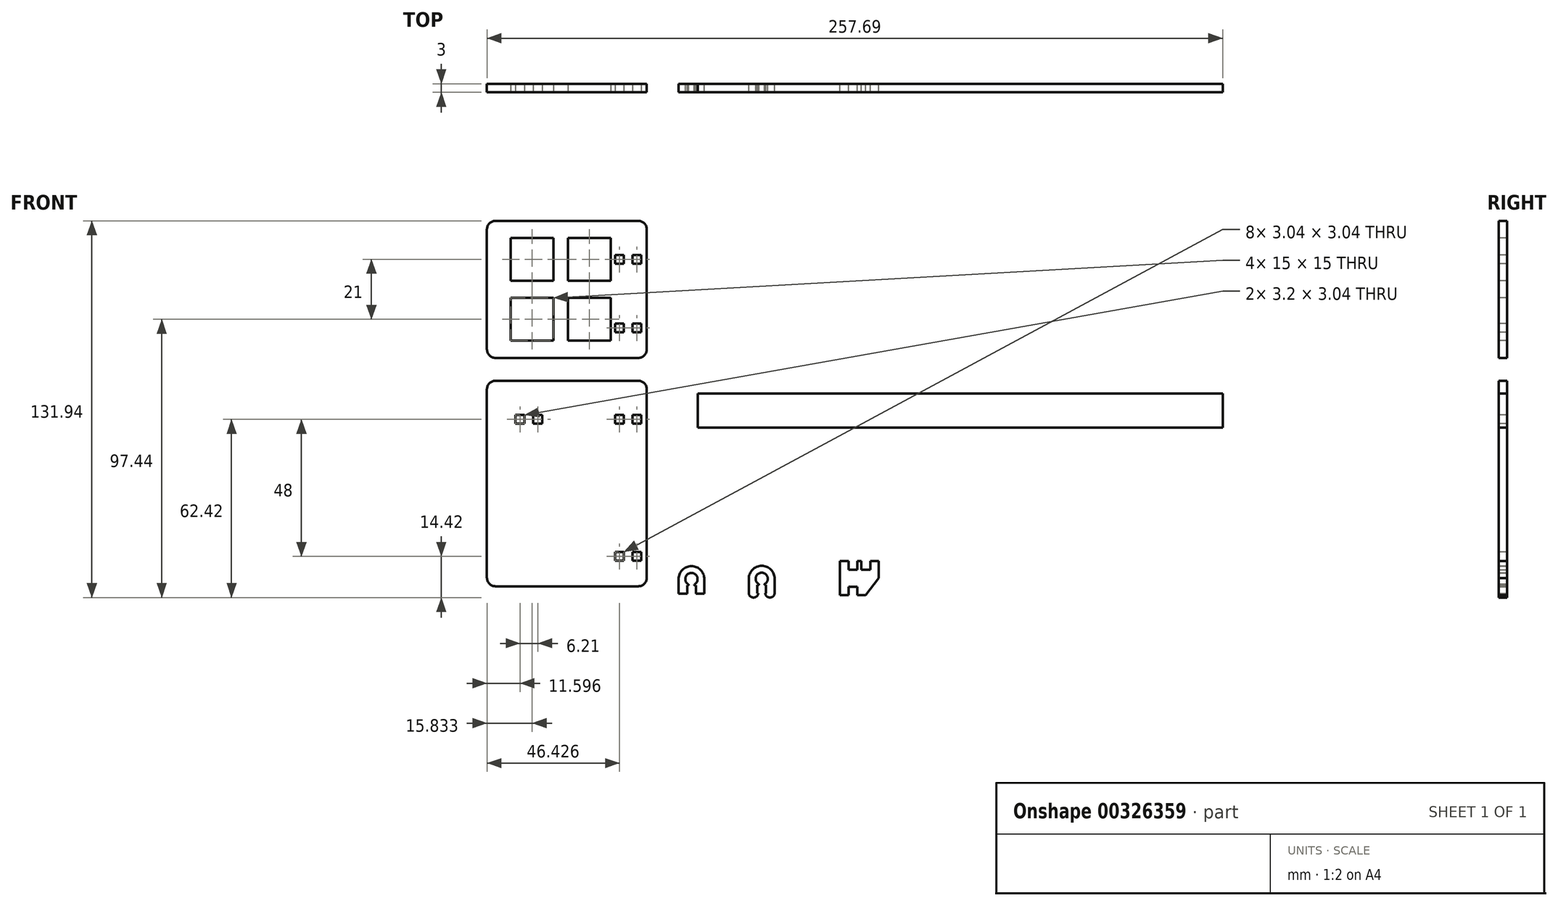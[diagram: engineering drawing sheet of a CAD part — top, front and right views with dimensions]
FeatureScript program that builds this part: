
annotation { "Feature Type Name" : "Feature", "Feature Type Description" : "" }
export const myFeature = defineFeature(function(context is Context, id is Id, definition is map)
    precondition{}
    {
        {
            var Q0;
            Q0=qCreatedBy(makeId("Front.planeOp"),FACE);
            var sketch = newSketch(context, id + "F0", { "sketchPlane" : qUnion([Q0])});
            skArc(sketch, "E0", {"start": v(1.01, 0.63) * mm, "mid": v(0.03, 4.67) * mm, "end": v(-1.07, 0.66) * mm});
            skPoint(sketch, "E0.centerSnap0", {"position": v(-1.52, 2.52) * mm});
            skArc(sketch, "E1", {"start": v(4.53, 2.52) * mm, "mid": v(0, 7.05) * mm, "end": v(-4.53, 2.52) * mm});
            skLineSegment(sketch, "E2", {"start": v(-4.53, 2.52) * mm, "end": v(-4.53, -2.63) * mm});
            skLineSegment(sketch, "E3", {"start": v(4.52, 2.52) * mm, "end": v(4.53, -2.63) * mm});
            skPoint(sketch, "E3.startSnap0", {"position": v(1.52, 2.52) * mm});
            skPoint(sketch, "E4.orphan", {"position": v(-1.52, 4.05) * mm});
            skPoint(sketch, "E5.orphan", {"position": v(1.52, 4.05) * mm});
            skLineSegment(sketch, "E6", {"start": v(-1.08, 0.37) * mm, "end": v(-1.52, 0.37) * mm});
            skLineSegment(sketch, "E7", {"start": v(1.07, 0.37) * mm, "end": v(1.53, 0.37) * mm});
            skArc(sketch, "E8", {"start": v(-1.08, 0.37) * mm, "mid": v(-1, 0.52) * mm, "end": v(-1.08, 0.67) * mm});
            skArc(sketch, "E9", {"start": v(1.01, 0.63) * mm, "mid": v(0.96, 0.47) * mm, "end": v(1.1, 0.37) * mm});
            skPoint(sketch, "E10.orphan", {"position": v(0, 0.37) * mm});
            skPoint(sketch, "E11.start.orphan", {"position": v(-2.15, 2.53) * mm});
            skPoint(sketch, "E12.start.orphan", {"position": v(2.15, 2.53) * mm});
            skLineSegment(sketch, "E13", {"start": v(-1.52, -2.63) * mm, "end": v(-1.52, 0.37) * mm});
            skLineSegment(sketch, "E14", {"start": v(1.53, -2.63) * mm, "end": v(1.53, 0.38) * mm});
            skPoint(sketch, "E15", {"position": v(-1.52, -2.63) * mm});
            skPoint(sketch, "E16", {"position": v(1.53, -2.63) * mm});
            skLineSegment(sketch, "E17", {"start": v(-1.52, -2.63) * mm, "end": v(-4.53, -2.63) * mm});
            skLineSegment(sketch, "E18", {"start": v(1.53, -2.63) * mm, "end": v(4.53, -2.63) * mm});
            skPoint(sketch, "E19.start.orphan", {"position": v(0, 4.05) * mm});
            skArc(sketch, "E20", {"start": v(25.62, 0.77) * mm, "mid": v(24.65, 4.77) * mm, "end": v(23.55, 0.8) * mm});
            skPoint(sketch, "E20.centerSnap0", {"position": v(23.09, 2.64) * mm});
            skArc(sketch, "E21", {"start": v(29.14, 2.67) * mm, "mid": v(24.6, 7.17) * mm, "end": v(20.09, 2.64) * mm});
            skLineSegment(sketch, "E22", {"start": v(20.09, 2.64) * mm, "end": v(20.09, -2.5) * mm});
            skLineSegment(sketch, "E23", {"start": v(29.14, 2.67) * mm, "end": v(29.14, -2.48) * mm});
            skPoint(sketch, "E23.startSnap0", {"position": v(26.14, 2.67) * mm});
            skPoint(sketch, "E24.orphan", {"position": v(23.08, 4.16) * mm});
            skPoint(sketch, "E25.orphan", {"position": v(26.12, 4.15) * mm});
            skLineSegment(sketch, "E26", {"start": v(23.55, 0.52) * mm, "end": v(23.09, 0.52) * mm});
            skLineSegment(sketch, "E27", {"start": v(25.68, 0.52) * mm, "end": v(26.14, 0.52) * mm});
            skArc(sketch, "E28", {"start": v(23.55, 0.52) * mm, "mid": v(23.63, 0.66) * mm, "end": v(23.55, 0.8) * mm});
            skArc(sketch, "E29", {"start": v(25.62, 0.77) * mm, "mid": v(25.56, 0.61) * mm, "end": v(25.7, 0.52) * mm});
            skPoint(sketch, "E30.orphan", {"position": v(24.61, 0.52) * mm});
            skPoint(sketch, "E31.start.orphan", {"position": v(22.49, 2.64) * mm});
            skPoint(sketch, "E32.start.orphan", {"position": v(26.74, 2.67) * mm});
            skLineSegment(sketch, "E33", {"start": v(23.09, -2.48) * mm, "end": v(23.09, 0.52) * mm});
            skLineSegment(sketch, "E34", {"start": v(26.14, -2.48) * mm, "end": v(26.14, 0.52) * mm});
            skPoint(sketch, "E35", {"position": v(23.09, -2.48) * mm});
            skPoint(sketch, "E36", {"position": v(26.14, -2.48) * mm});
            skPoint(sketch, "E37.start.orphan", {"position": v(24.6, 4.15) * mm});
            skPoint(sketch, "E38.end.orphan", {"position": v(23.09, -3.5) * mm});
            skPoint(sketch, "E39.orphan", {"position": v(26.14, -3.48) * mm});
            skLineSegment(sketch, "E40", {"start": v(23.09, -2.48) * mm, "end": v(23.39, -2.48) * mm});
            skLineSegment(sketch, "E41", {"start": v(26.14, -2.48) * mm, "end": v(25.84, -2.48) * mm});
            skArc(sketch, "E42", {"start": v(20.09, -2.5) * mm, "mid": v(21.74, -3.94) * mm, "end": v(23.39, -2.48) * mm});
            skArc(sketch, "E43", {"start": v(25.84, -2.48) * mm, "mid": v(27.49, -3.94) * mm, "end": v(29.14, -2.48) * mm});
            skLineSegment(sketch, "E44", {"start": v(61.04, -3.15) * mm, "end": v(58.06, -3.15) * mm});
            skLineSegment(sketch, "E45", {"start": v(58.06, -3.15) * mm, "end": v(58.06, -0.13) * mm});
            skLineSegment(sketch, "E46", {"start": v(58.06, -0.13) * mm, "end": v(55.02, -0.13) * mm});
            skLineSegment(sketch, "E47", {"start": v(55.02, -0.13) * mm, "end": v(55.02, -3.15) * mm});
            skLineSegment(sketch, "E48", {"start": v(55.02, -3.15) * mm, "end": v(52.04, -3.15) * mm});
            skLineSegment(sketch, "E49", {"start": v(52.04, -3.15) * mm, "end": v(52.04, 8.85) * mm});
            skLineSegment(sketch, "E50", {"start": v(52.04, 8.85) * mm, "end": v(55.02, 8.85) * mm});
            skLineSegment(sketch, "E51", {"start": v(55.02, 8.85) * mm, "end": v(55.02, 5.83) * mm});
            skLineSegment(sketch, "E52", {"start": v(55.02, 5.83) * mm, "end": v(58.06, 5.83) * mm});
            skLineSegment(sketch, "E53", {"start": v(58.06, 5.83) * mm, "end": v(58.06, 8.85) * mm});
            skLineSegment(sketch, "E54", {"start": v(58.06, 8.85) * mm, "end": v(59.5, 8.85) * mm});
            skPoint(sketch, "E55", {"position": v(59.5, 8.85) * mm});
            skPoint(sketch, "E56", {"position": v(59.5, -3.15) * mm});
            skPoint(sketch, "E57", {"position": v(62.6, 8.85) * mm});
            skPoint(sketch, "E58.orphan", {"position": v(61.04, 8.85) * mm});
            skLineSegment(sketch, "E59", {"start": v(62.6, 8.85) * mm, "end": v(65.6, 8.85) * mm});
            skLineSegment(sketch, "E60", {"start": v(65.6, 8.85) * mm, "end": v(65.6, 2.85) * mm});
            skLineSegment(sketch, "E61", {"start": v(65.6, 2.85) * mm, "end": v(61.04, -3.15) * mm});
            skLineSegment(sketch, "E62", {"start": v(59.5, 8.85) * mm, "end": v(59.5, 5.81) * mm});
            skLineSegment(sketch, "E63", {"start": v(59.5, 5.81) * mm, "end": v(62.6, 5.81) * mm});
            skLineSegment(sketch, "E64", {"start": v(62.6, 5.81) * mm, "end": v(62.6, 8.85) * mm});
            skSolve(sketch);
        }
        {
            var Q0;
            Q0=makeQuery(id+"F0.imprint","IMPRINT",FACE,{"disambiguationData":[TD([[makeQuery(id+"F0.imprint","IMPRINT",EDGE,{"derivedFrom":sQuery(id+"F0.wireOp",EDGE,"E0")}),-1.0]])]});
            var Q1;
            {var subQ1=sQuery(id+"F0.wireOp",EDGE,"E20");Q1=makeQuery(id+"F0.imprint","IMPRINT",FACE,{"disambiguationData":[TD([[makeQuery(id+"F0.imprint","IMPRINT",EDGE,{"derivedFrom":subQ1}),-1.0]])]});}
            var Q2;
            Q2=makeQuery(id+"F0.imprint","IMPRINT",FACE,{"disambiguationData":[TD([[makeQuery(id+"F0.imprint","IMPRINT",EDGE,{"derivedFrom":sQuery(id+"F0.wireOp",EDGE,"E44")}),-1.0]])]});
            extrude(context, id + "F1", {"entities" : qUnion([Q0, Q1, Q2]), "depth" : 3 * mm});
        }
        {
            var Q0;
            Q0=qCreatedBy(makeId("Front.planeOp"),FACE);
            var sketch = newSketch(context, id + "F2", { "sketchPlane" : qUnion([Q0])});
            skLineSegment(sketch, "E65.bottom", {"start": v(-71.63, 0) * mm, "end": v(-15.63, 0) * mm});
            skLineSegment(sketch, "E65.left", {"start": v(-71.63, 0) * mm, "end": v(-71.63, 72) * mm});
            skLineSegment(sketch, "E65.right", {"start": v(-15.63, 0) * mm, "end": v(-15.63, 72) * mm});
            skLineSegment(sketch, "E66", {"start": v(-71.63, 80) * mm, "end": v(-71.63, 128) * mm});
            skLineSegment(sketch, "E67", {"start": v(-15.63, 80) * mm, "end": v(-15.63, 128) * mm});
            skLineSegment(sketch, "E68", {"start": v(-15.63, 128) * mm, "end": v(-71.63, 128) * mm});
            skLineSegment(sketch, "E69", {"start": v(-71.63, 72) * mm, "end": v(-15.63, 72) * mm});
            skLineSegment(sketch, "E70", {"start": v(-71.63, 80) * mm, "end": v(-15.63, 80) * mm});
            skSolve(sketch);
        }
        {
            var Q0;
            Q0=makeQuery(id+"F2.imprint","IMPRINT",FACE,{"disambiguationData":[TD([[makeQuery(id+"F2.imprint","IMPRINT",EDGE,{"derivedFrom":sQuery(id+"F2.wireOp",EDGE,"E66")}),-1.0]])]});
            var Q1;
            Q1=makeQuery(id+"F2.imprint","IMPRINT",FACE,{"disambiguationData":[TD([[makeQuery(id+"F2.imprint","IMPRINT",EDGE,{"derivedFrom":sQuery(id+"F2.wireOp",EDGE,"E65.bottom")}),1.0]])]});
            extrude(context, id + "F3", {"entities" : qUnion([Q0, Q1]), "depth" : 3 * mm});
        }
        {
            var Q0;
            Q0=makeQuery(id+"F3.opExtrude","CAP_FACE",FACE,{"disambiguationData":[OSD([sQuery(id+"F2.wireOp",EDGE,"E66"),sQuery(id+"F2.wireOp",EDGE,"E67"),sQuery(id+"F2.wireOp",EDGE,"E68"),sQuery(id+"F2.wireOp",EDGE,"E70")])],"isStart":false});
            var sketch = newSketch(context, id + "F4", { "sketchPlane" : qUnion([Q0])});
            skLineSegment(sketch, "E71.bottom", {"start": v(-23.68, 12) * mm, "end": v(-26.72, 12) * mm});
            skLineSegment(sketch, "E71.top", {"start": v(-23.68, 8.96) * mm, "end": v(-26.72, 8.96) * mm});
            skLineSegment(sketch, "E71.left", {"start": v(-23.68, 12) * mm, "end": v(-23.68, 8.96) * mm});
            skLineSegment(sketch, "E71.right", {"start": v(-26.72, 12) * mm, "end": v(-26.72, 8.96) * mm});
            skLineSegment(sketch, "E72.bottom", {"start": v(-20.67, 12) * mm, "end": v(-17.63, 12) * mm});
            skLineSegment(sketch, "E72.top", {"start": v(-20.67, 8.96) * mm, "end": v(-17.63, 8.96) * mm});
            skLineSegment(sketch, "E72.left", {"start": v(-20.67, 12) * mm, "end": v(-20.67, 8.96) * mm});
            skLineSegment(sketch, "E72.right", {"start": v(-17.63, 12) * mm, "end": v(-17.63, 8.96) * mm});
            skLineSegment(sketch, "E73.bottom", {"start": v(-23.68, 60) * mm, "end": v(-26.72, 60) * mm});
            skLineSegment(sketch, "E73.top", {"start": v(-23.68, 56.96) * mm, "end": v(-26.72, 56.96) * mm});
            skLineSegment(sketch, "E73.left", {"start": v(-23.68, 60) * mm, "end": v(-23.68, 56.96) * mm});
            skLineSegment(sketch, "E73.right", {"start": v(-26.72, 60) * mm, "end": v(-26.72, 56.96) * mm});
            skLineSegment(sketch, "E74.bottom", {"start": v(-20.67, 60) * mm, "end": v(-17.63, 60) * mm});
            skLineSegment(sketch, "E74.top", {"start": v(-20.67, 56.96) * mm, "end": v(-17.63, 56.96) * mm});
            skLineSegment(sketch, "E74.left", {"start": v(-20.67, 60) * mm, "end": v(-20.67, 56.96) * mm});
            skLineSegment(sketch, "E74.right", {"start": v(-17.63, 60) * mm, "end": v(-17.63, 56.96) * mm});
            skLineSegment(sketch, "E75.bottom", {"start": v(-23.68, 92) * mm, "end": v(-26.72, 92) * mm});
            skLineSegment(sketch, "E75.top", {"start": v(-23.68, 88.96) * mm, "end": v(-26.72, 88.96) * mm});
            skLineSegment(sketch, "E75.left", {"start": v(-23.68, 92) * mm, "end": v(-23.68, 88.96) * mm});
            skLineSegment(sketch, "E75.right", {"start": v(-26.72, 92) * mm, "end": v(-26.72, 88.96) * mm});
            skLineSegment(sketch, "E76.bottom", {"start": v(-20.67, 92) * mm, "end": v(-17.63, 92) * mm});
            skLineSegment(sketch, "E76.top", {"start": v(-20.67, 88.96) * mm, "end": v(-17.63, 88.96) * mm});
            skLineSegment(sketch, "E76.left", {"start": v(-20.67, 92) * mm, "end": v(-20.67, 88.96) * mm});
            skLineSegment(sketch, "E76.right", {"start": v(-17.63, 92) * mm, "end": v(-17.63, 88.96) * mm});
            skLineSegment(sketch, "E77.bottom", {"start": v(-23.68, 116) * mm, "end": v(-26.72, 116) * mm});
            skLineSegment(sketch, "E77.top", {"start": v(-23.68, 112.96) * mm, "end": v(-26.72, 112.96) * mm});
            skLineSegment(sketch, "E77.left", {"start": v(-23.68, 116) * mm, "end": v(-23.68, 112.96) * mm});
            skLineSegment(sketch, "E77.right", {"start": v(-26.72, 116) * mm, "end": v(-26.72, 112.96) * mm});
            skLineSegment(sketch, "E78.bottom", {"start": v(-20.67, 116) * mm, "end": v(-17.63, 116) * mm});
            skLineSegment(sketch, "E78.top", {"start": v(-20.67, 112.96) * mm, "end": v(-17.63, 112.96) * mm});
            skLineSegment(sketch, "E78.left", {"start": v(-20.67, 116) * mm, "end": v(-20.67, 112.96) * mm});
            skLineSegment(sketch, "E78.right", {"start": v(-17.63, 116) * mm, "end": v(-17.63, 112.96) * mm});
            skLineSegment(sketch, "E79.bottom", {"start": v(-58.43, 60) * mm, "end": v(-61.63, 60) * mm});
            skLineSegment(sketch, "E79.top", {"start": v(-58.43, 56.96) * mm, "end": v(-61.63, 56.96) * mm});
            skLineSegment(sketch, "E79.left", {"start": v(-58.43, 60) * mm, "end": v(-58.43, 56.96) * mm});
            skLineSegment(sketch, "E79.right", {"start": v(-61.63, 60) * mm, "end": v(-61.63, 56.96) * mm});
            skLineSegment(sketch, "E80.bottom", {"start": v(-55.42, 60) * mm, "end": v(-52.22, 60) * mm});
            skLineSegment(sketch, "E80.top", {"start": v(-55.42, 56.96) * mm, "end": v(-52.22, 56.96) * mm});
            skLineSegment(sketch, "E80.left", {"start": v(-55.42, 60) * mm, "end": v(-55.42, 56.96) * mm});
            skLineSegment(sketch, "E80.right", {"start": v(-52.22, 60) * mm, "end": v(-52.22, 56.96) * mm});
            skSolve(sketch);
        }
        {
            var Q0;
            Q0=makeQuery(id+"F4.imprint","IMPRINT",FACE,{"disambiguationData":[TD([[makeQuery(id+"F4.imprint","IMPRINT",EDGE,{"derivedFrom":sQuery(id+"F4.wireOp",EDGE,"E77.bottom")}),1.0]])]});
            var Q1;
            Q1=makeQuery(id+"F4.imprint","IMPRINT",FACE,{"disambiguationData":[TD([[makeQuery(id+"F4.imprint","IMPRINT",EDGE,{"derivedFrom":sQuery(id+"F4.wireOp",EDGE,"E78.bottom")}),-1.0]])]});
            var Q2;
            Q2=makeQuery(id+"F4.imprint","IMPRINT",FACE,{"disambiguationData":[TD([[makeQuery(id+"F4.imprint","IMPRINT",EDGE,{"derivedFrom":sQuery(id+"F4.wireOp",EDGE,"E75.bottom")}),1.0]])]});
            var Q3;
            Q3=makeQuery(id+"F4.imprint","IMPRINT",FACE,{"disambiguationData":[TD([[makeQuery(id+"F4.imprint","IMPRINT",EDGE,{"derivedFrom":sQuery(id+"F4.wireOp",EDGE,"E76.bottom")}),-1.0]])]});
            var Q4;
            Q4=makeQuery(id+"F4.imprint","IMPRINT",FACE,{"disambiguationData":[TD([[makeQuery(id+"F4.imprint","IMPRINT",EDGE,{"derivedFrom":sQuery(id+"F4.wireOp",EDGE,"E73.bottom")}),1.0]])]});
            var Q5;
            Q5=makeQuery(id+"F4.imprint","IMPRINT",FACE,{"disambiguationData":[TD([[makeQuery(id+"F4.imprint","IMPRINT",EDGE,{"derivedFrom":sQuery(id+"F4.wireOp",EDGE,"E74.bottom")}),-1.0]])]});
            var Q6;
            Q6=makeQuery(id+"F4.imprint","IMPRINT",FACE,{"disambiguationData":[TD([[makeQuery(id+"F4.imprint","IMPRINT",EDGE,{"derivedFrom":sQuery(id+"F4.wireOp",EDGE,"E71.bottom")}),1.0]])]});
            var Q7;
            Q7=makeQuery(id+"F4.imprint","IMPRINT",FACE,{"disambiguationData":[TD([[makeQuery(id+"F4.imprint","IMPRINT",EDGE,{"derivedFrom":sQuery(id+"F4.wireOp",EDGE,"E72.bottom")}),-1.0]])]});
            extrude(context, id + "F5", {"entities" : qUnion([Q0, Q1, Q2, Q3, Q4, Q5, Q6, Q7]), "operationType" : NewBodyOperationType.REMOVE, "endBound" : BoundingType.THROUGH_ALL, "oppositeDirection" : true, "depth" : 25 * mm});
        }
        {
            var Q0;
            Q0=qSketchRegion(id+"F4",true);
            extrude(context, id + "F6", {"entities" : qUnion([Q0]), "operationType" : NewBodyOperationType.REMOVE, "oppositeDirection" : true, "depth" : 25 * mm});
        }
        {
            var Q0;
            Q0=makeQuery(id+"F3.opExtrude","CAP_FACE",FACE,{"disambiguationData":[OSD([sQuery(id+"F2.wireOp",EDGE,"E66"),sQuery(id+"F2.wireOp",EDGE,"E67"),sQuery(id+"F2.wireOp",EDGE,"E68"),sQuery(id+"F2.wireOp",EDGE,"E70")])],"isStart":false});
            var sketch = newSketch(context, id + "F7", { "sketchPlane" : qUnion([Q0])});
            skLineSegment(sketch, "E81.bottom", {"start": v(-63.3, 122) * mm, "end": v(-48.3, 122) * mm});
            skLineSegment(sketch, "E81.top", {"start": v(-63.3, 107) * mm, "end": v(-48.3, 107) * mm});
            skLineSegment(sketch, "E81.left", {"start": v(-63.3, 122) * mm, "end": v(-63.3, 107) * mm});
            skLineSegment(sketch, "E81.right", {"start": v(-48.3, 122) * mm, "end": v(-48.3, 107) * mm});
            skLineSegment(sketch, "E82.bottom", {"start": v(-43.3, 122) * mm, "end": v(-28.3, 122) * mm});
            skLineSegment(sketch, "E82.top", {"start": v(-43.3, 107) * mm, "end": v(-28.3, 107) * mm});
            skLineSegment(sketch, "E82.left", {"start": v(-43.3, 122) * mm, "end": v(-43.3, 107) * mm});
            skLineSegment(sketch, "E82.right", {"start": v(-28.3, 122) * mm, "end": v(-28.3, 107) * mm});
            skLineSegment(sketch, "E83.bottom", {"start": v(-63.3, 101) * mm, "end": v(-48.3, 101) * mm});
            skLineSegment(sketch, "E83.top", {"start": v(-63.3, 86) * mm, "end": v(-48.3, 86) * mm});
            skLineSegment(sketch, "E83.left", {"start": v(-63.3, 101) * mm, "end": v(-63.3, 86) * mm});
            skLineSegment(sketch, "E83.right", {"start": v(-48.3, 101) * mm, "end": v(-48.3, 86) * mm});
            skLineSegment(sketch, "E84.bottom", {"start": v(-43.3, 101) * mm, "end": v(-28.3, 101) * mm});
            skLineSegment(sketch, "E84.top", {"start": v(-43.3, 86) * mm, "end": v(-28.3, 86) * mm});
            skLineSegment(sketch, "E84.left", {"start": v(-43.3, 101) * mm, "end": v(-43.3, 86) * mm});
            skLineSegment(sketch, "E84.right", {"start": v(-28.3, 101) * mm, "end": v(-28.3, 86) * mm});
            skSolve(sketch);
        }
        {
            var Q0;
            Q0=makeQuery(id+"F7.imprint","IMPRINT",FACE,{"disambiguationData":[TD([[makeQuery(id+"F7.imprint","IMPRINT",EDGE,{"derivedFrom":sQuery(id+"F7.wireOp",EDGE,"E81.bottom")}),-1.0]])]});
            var Q1;
            Q1=makeQuery(id+"F7.imprint","IMPRINT",FACE,{"disambiguationData":[TD([[makeQuery(id+"F7.imprint","IMPRINT",EDGE,{"derivedFrom":sQuery(id+"F7.wireOp",EDGE,"E82.bottom")}),-1.0]])]});
            var Q2;
            Q2=makeQuery(id+"F7.imprint","IMPRINT",FACE,{"disambiguationData":[TD([[makeQuery(id+"F7.imprint","IMPRINT",EDGE,{"derivedFrom":sQuery(id+"F7.wireOp",EDGE,"E84.bottom")}),-1.0]])]});
            var Q3;
            Q3=makeQuery(id+"F7.imprint","IMPRINT",FACE,{"disambiguationData":[TD([[makeQuery(id+"F7.imprint","IMPRINT",EDGE,{"derivedFrom":sQuery(id+"F7.wireOp",EDGE,"E83.bottom")}),-1.0]])]});
            extrude(context, id + "F8", {"entities" : qUnion([Q0, Q1, Q2, Q3]), "operationType" : NewBodyOperationType.REMOVE, "endBound" : BoundingType.THROUGH_ALL, "oppositeDirection" : true, "depth" : 25 * mm});
        }
        {
            var Q0;
            Q0=makeQuery(id+"F3.opExtrude","SWEPT_EDGE",EDGE,{"disambiguationData":[OSD([sQuery(id+"F2.wireOp",EDGE,"E66"),sQuery(id+"F2.wireOp",EDGE,"E68")])]});
            var Q1;
            Q1=makeQuery(id+"F3.opExtrude","SWEPT_EDGE",EDGE,{"disambiguationData":[OSD([sQuery(id+"F2.wireOp",EDGE,"E65.left"),sQuery(id+"F2.wireOp",EDGE,"E69")])]});
            var Q2;
            Q2=makeQuery(id+"F3.opExtrude","SWEPT_EDGE",EDGE,{"disambiguationData":[OSD([sQuery(id+"F2.wireOp",EDGE,"E65.right"),sQuery(id+"F2.wireOp",EDGE,"E69")])]});
            var Q3;
            Q3=makeQuery(id+"F3.opExtrude","SWEPT_EDGE",EDGE,{"disambiguationData":[OSD([sQuery(id+"F2.wireOp",EDGE,"E66"),sQuery(id+"F2.wireOp",EDGE,"E70")])]});
            var Q4;
            Q4=makeQuery(id+"F3.opExtrude","SWEPT_EDGE",EDGE,{"disambiguationData":[OSD([sQuery(id+"F2.wireOp",EDGE,"E67"),sQuery(id+"F2.wireOp",EDGE,"E70")])]});
            var Q5;
            Q5=makeQuery(id+"F3.opExtrude","SWEPT_EDGE",EDGE,{"disambiguationData":[OSD([sQuery(id+"F2.wireOp",EDGE,"E67"),sQuery(id+"F2.wireOp",EDGE,"E68")])]});
            var Q6;
            Q6=makeQuery(id+"F3.opExtrude","SWEPT_EDGE",EDGE,{"disambiguationData":[OSD([sQuery(id+"F2.wireOp",EDGE,"E65.bottom"),sQuery(id+"F2.wireOp",EDGE,"E65.left")])]});
            var Q7;
            Q7=makeQuery(id+"F3.opExtrude","SWEPT_EDGE",EDGE,{"disambiguationData":[OSD([sQuery(id+"F2.wireOp",EDGE,"E65.bottom"),sQuery(id+"F2.wireOp",EDGE,"E65.right")])]});
            fillet(context, id + "F9", {"entities" : qUnion([Q0, Q1, Q2, Q3, Q4, Q5, Q6, Q7]), "radius" : 3 * mm, "tangentPropagation" : true, "allowEdgeOverflow" : false});
        }
        {
            var Q0;
            Q0=qCreatedBy(makeId("Front.planeOp"),FACE);
            var sketch = newSketch(context, id + "F10", { "sketchPlane" : qUnion([Q0])});
            skLineSegment(sketch, "E85.bottom", {"start": v(2.2, 55.55) * mm, "end": v(186.06, 55.55) * mm});
            skLineSegment(sketch, "E85.top", {"start": v(2.2, 67.47) * mm, "end": v(186.06, 67.47) * mm});
            skLineSegment(sketch, "E85.left", {"start": v(2.2, 55.55) * mm, "end": v(2.2, 67.47) * mm});
            skLineSegment(sketch, "E85.right", {"start": v(186.06, 55.55) * mm, "end": v(186.06, 67.47) * mm});
            skSolve(sketch);
        }
        {
            var Q0;
            Q0=makeQuery(id+"F10.imprint","IMPRINT",FACE,{"disambiguationData":[TD([[makeQuery(id+"F10.imprint","IMPRINT",EDGE,{"derivedFrom":sQuery(id+"F10.wireOp",EDGE,"E85.bottom")}),1.0]])]});
            extrude(context, id + "F11", {"entities" : qUnion([Q0]), "depth" : 3 * mm});
        }
    });
